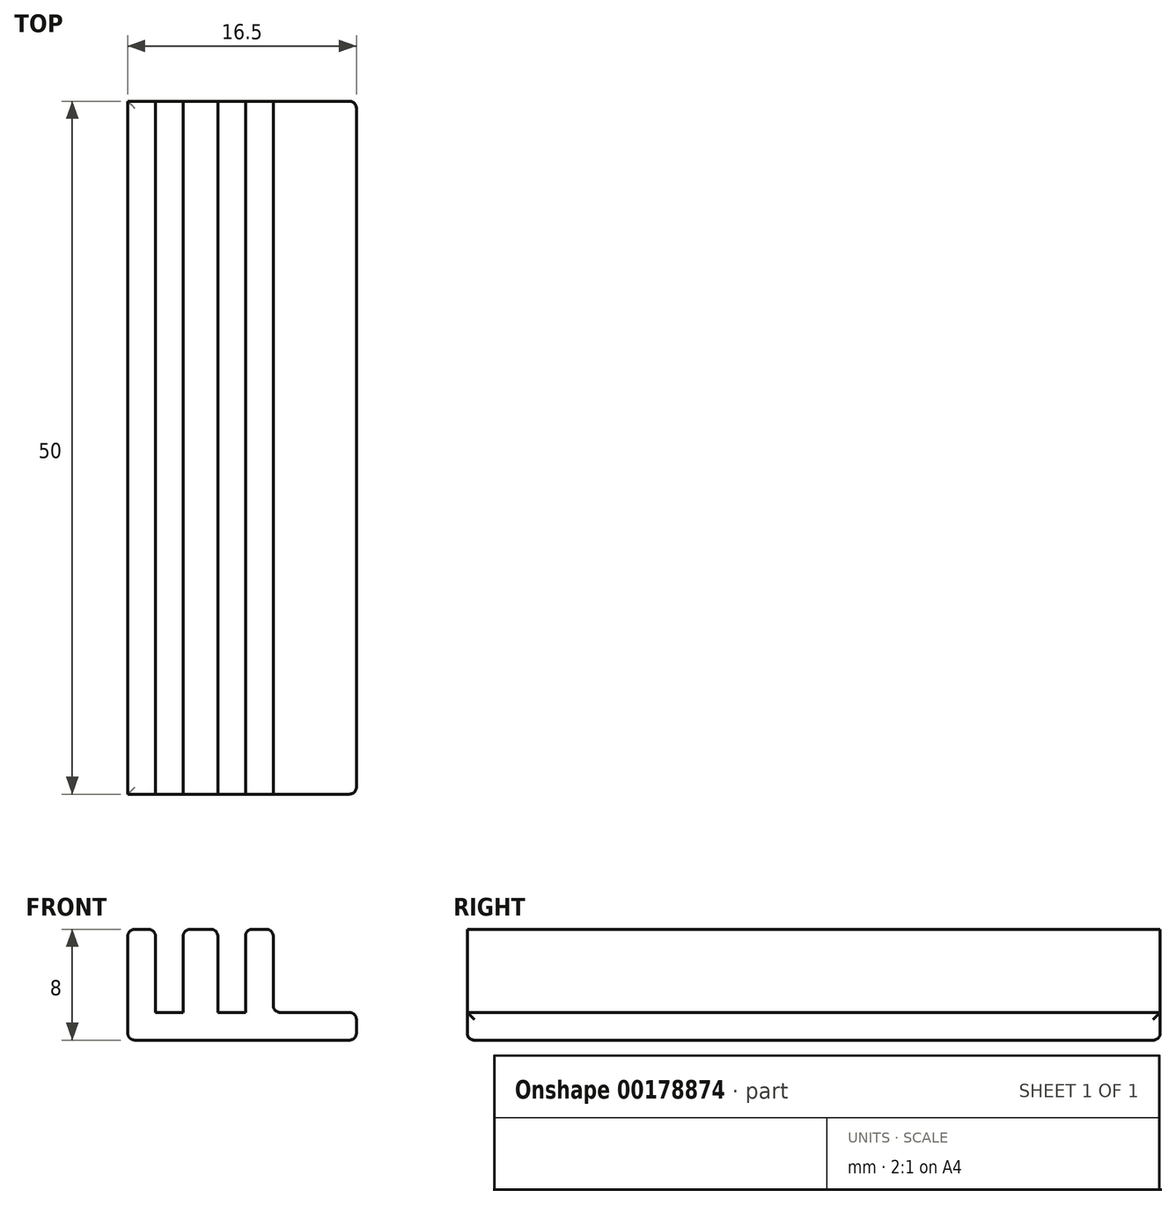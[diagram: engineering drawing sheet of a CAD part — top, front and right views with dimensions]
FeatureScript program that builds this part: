
annotation { "Feature Type Name" : "Feature", "Feature Type Description" : "" }
export const myFeature = defineFeature(function(context is Context, id is Id, definition is map)
    precondition{}
    {
        {
            var Q0;
            Q0=qCreatedBy(makeId("Front.planeOp"),FACE);
            var sketch = newSketch(context, id + "F0", { "sketchPlane" : qUnion([Q0])});
            skLineSegment(sketch, "E0", {"start": v(0, 0) * mm, "end": v(16.5, 0) * mm});
            skLineSegment(sketch, "E1", {"start": v(0, 0) * mm, "end": v(0, 8) * mm});
            skLineSegment(sketch, "E2", {"start": v(0, 8) * mm, "end": v(2, 8) * mm});
            skLineSegment(sketch, "E3", {"start": v(2, 8) * mm, "end": v(2, 2) * mm});
            skLineSegment(sketch, "E4", {"start": v(2, 2) * mm, "end": v(4, 2) * mm});
            skLineSegment(sketch, "E5", {"start": v(4, 2) * mm, "end": v(4, 8) * mm});
            skLineSegment(sketch, "E6", {"start": v(4, 8) * mm, "end": v(6.5, 8) * mm});
            skLineSegment(sketch, "E7", {"start": v(6.5, 8) * mm, "end": v(6.5, 2) * mm});
            skLineSegment(sketch, "E8", {"start": v(6.5, 2) * mm, "end": v(8.5, 2) * mm});
            skLineSegment(sketch, "E9", {"start": v(8.5, 2) * mm, "end": v(8.5, 8) * mm});
            skLineSegment(sketch, "E10", {"start": v(8.5, 8) * mm, "end": v(10.5, 8) * mm});
            skLineSegment(sketch, "E11", {"start": v(10.5, 8) * mm, "end": v(10.5, 2) * mm});
            skLineSegment(sketch, "E12", {"start": v(10.5, 2) * mm, "end": v(16.5, 2) * mm});
            skLineSegment(sketch, "E13", {"start": v(16.5, 2) * mm, "end": v(16.5, 0) * mm});
            skSolve(sketch);
        }
        {
            var Q0;
            Q0 = qSketchRegion(id + "F0", true);
            extrude(context, id + "F1", {"entities" : qUnion([Q0]), "depth" : 50 * mm});
        }
        {
            var Q0;
            Q0=makeQuery(id+"F1.opExtrude","SWEPT_FACE",FACE,{"disambiguationData":[OSD([sQuery(id+"F0.wireOp",EDGE,"E13")])]});
            fillet(context, id + "F2", {"entities" : qUnion([Q0]), "radius" : 0.5 * mm, "tangentPropagation" : true, "allowEdgeOverflow" : false});
        }
        {
            var Q0;
            Q0=makeQuery(id+"F1.opExtrude","SWEPT_EDGE",EDGE,{"disambiguationData":[OSD([sQuery(id+"F0.wireOp",EDGE,"E9"),sQuery(id+"F0.wireOp",EDGE,"E10")])]});
            var Q1;
            Q1=makeQuery(id+"F1.opExtrude","SWEPT_EDGE",EDGE,{"disambiguationData":[OSD([sQuery(id+"F0.wireOp",EDGE,"E10"),sQuery(id+"F0.wireOp",EDGE,"E11")])]});
            var Q2;
            Q2=makeQuery(id+"F1.opExtrude","SWEPT_EDGE",EDGE,{"disambiguationData":[OSD([sQuery(id+"F0.wireOp",EDGE,"E6"),sQuery(id+"F0.wireOp",EDGE,"E7")])]});
            var Q3;
            Q3=makeQuery(id+"F1.opExtrude","SWEPT_EDGE",EDGE,{"disambiguationData":[OSD([sQuery(id+"F0.wireOp",EDGE,"E5"),sQuery(id+"F0.wireOp",EDGE,"E6")])]});
            var Q4;
            Q4=makeQuery(id+"F1.opExtrude","SWEPT_EDGE",EDGE,{"disambiguationData":[OSD([sQuery(id+"F0.wireOp",EDGE,"E2"),sQuery(id+"F0.wireOp",EDGE,"E3")])]});
            var Q5;
            Q5=makeQuery(id+"F1.opExtrude","SWEPT_EDGE",EDGE,{"disambiguationData":[OSD([sQuery(id+"F0.wireOp",EDGE,"E1"),sQuery(id+"F0.wireOp",EDGE,"E2")])]});
            fillet(context, id + "F3", {"entities" : qUnion([Q0, Q1, Q2, Q3, Q4, Q5]), "radius" : 0.5 * mm, "tangentPropagation" : true, "allowEdgeOverflow" : false});
        }
        {
            var Q0;
            Q0=makeQuery(id+"F1.opExtrude","SWEPT_FACE",FACE,{"disambiguationData":[OSD([sQuery(id+"F0.wireOp",EDGE,"E0")])]});
            fillet(context, id + "F4", {"entities" : qUnion([Q0]), "radius" : 0.5 * mm, "tangentPropagation" : true, "allowEdgeOverflow" : false});
        }
        {
            var Q0;
            Q0=makeQuery(id+"F1.opExtrude","SWEPT_EDGE",EDGE,{"disambiguationData":[OSD([sQuery(id+"F0.wireOp",EDGE,"E11"),sQuery(id+"F0.wireOp",EDGE,"E12")])]});
            fillet(context, id + "F5", {"entities" : qUnion([Q0]), "radius" : 0.5 * mm, "tangentPropagation" : true, "allowEdgeOverflow" : false});
        }
    });
